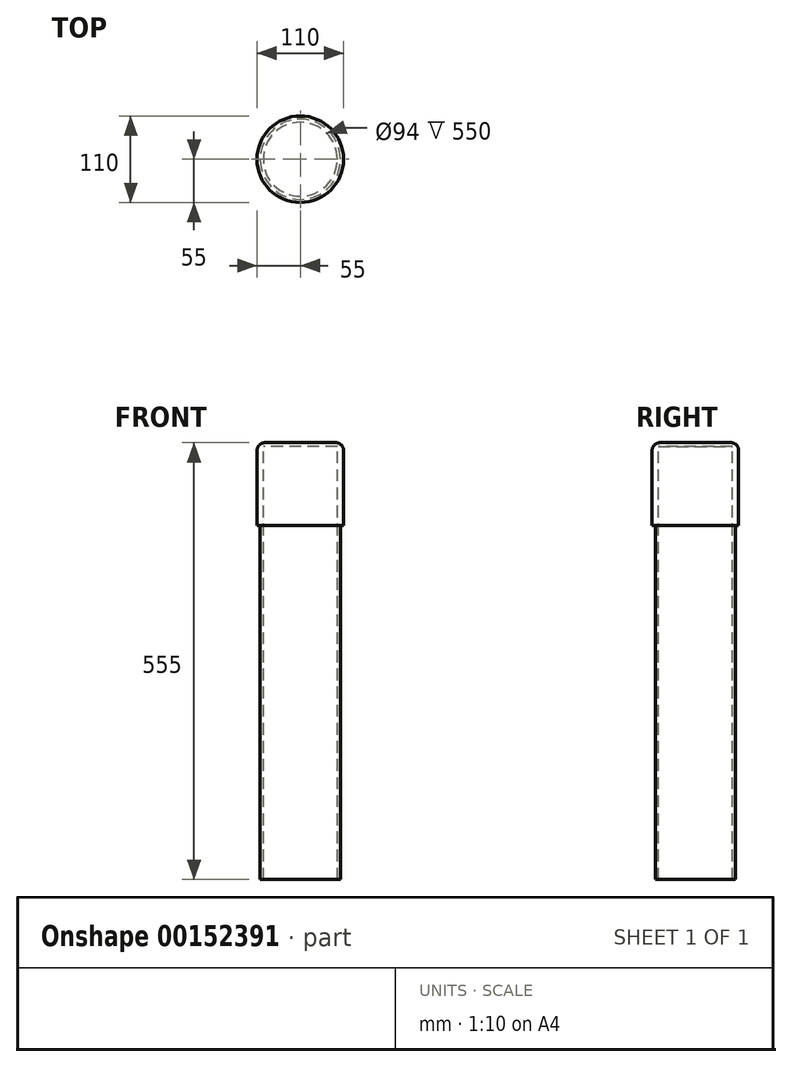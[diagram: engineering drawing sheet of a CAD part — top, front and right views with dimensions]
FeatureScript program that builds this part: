
annotation { "Feature Type Name" : "Feature", "Feature Type Description" : "" }
export const myFeature = defineFeature(function(context is Context, id is Id, definition is map)
    precondition{}
    {
        {
            var Q0;
            Q0=qCreatedBy(makeId("Top.planeOp"),FACE);
            var sketch = newSketch(context, id + "F0", { "sketchPlane" : qUnion([Q0])});
            skCircle(sketch, "E0", {"center": v(0, 0) * mm, "radius": 55 * mm});
            skCircle(sketch, "E1", {"center": v(0, 0) * mm, "radius": 51 * mm});
            skCircle(sketch, "E2", {"center": v(0, 0) * mm, "radius": 47 * mm});
            skSolve(sketch);
        }
        {
            var Q0;
            Q0=makeQuery(id+"F0.imprint","IMPRINT",FACE,{"disambiguationData":[TD([[makeQuery(id+"F0.imprint","IMPRINT",EDGE,{"derivedFrom":sQuery(id+"F0.wireOp",EDGE,"E1")}),1.0]])]});
            var Q1;
            Q1=makeQuery(id+"F0.imprint","IMPRINT",FACE,{"disambiguationData":[TD([[makeQuery(id+"F0.imprint","IMPRINT",EDGE,{"derivedFrom":sQuery(id+"F0.wireOp",EDGE,"E0")}),1.0]])]});
            var Q2;
            Q2=makeQuery(id+"F0.imprint","IMPRINT",FACE,{"disambiguationData":[TD([[makeQuery(id+"F0.imprint","IMPRINT",EDGE,{"derivedFrom":sQuery(id+"F0.wireOp",EDGE,"E2")}),1.0]])]});
            extrude(context, id + "F1", {"entities" : qUnion([Q0, Q1, Q2]), "depth" : 5 * mm});
        }
        {
            var Q0;
            Q0=makeQuery(id+"F0.imprint","IMPRINT",FACE,{"disambiguationData":[TD([[makeQuery(id+"F0.imprint","IMPRINT",EDGE,{"derivedFrom":sQuery(id+"F0.wireOp",EDGE,"E1")}),1.0]])]});
            extrude(context, id + "F2", {"entities" : qUnion([Q0]), "operationType" : NewBodyOperationType.ADD, "oppositeDirection" : true, "depth" : 50 * mm});
        }
        {
            var Q0;
            Q0=makeQuery(id+"F0.imprint","IMPRINT",FACE,{"disambiguationData":[TD([[makeQuery(id+"F0.imprint","IMPRINT",EDGE,{"derivedFrom":sQuery(id+"F0.wireOp",EDGE,"E0")}),1.0]])]});
            extrude(context, id + "F3", {"entities" : qUnion([Q0]), "operationType" : NewBodyOperationType.ADD, "oppositeDirection" : true, "depth" : 100 * mm});
        }
        {
            var Q0;
            Q0=makeQuery(id+"F1.opExtrude","CAP_EDGE",EDGE,{"disambiguationData":[OSD([sQuery(id+"F0.wireOp",EDGE,"E0")])],"isStart":false});
            fillet(context, id + "F4", {"entities" : qUnion([Q0]), "radius" : 10 * mm, "tangentPropagation" : true, "allowEdgeOverflow" : false});
        }
        {
            var Q0;
            Q0=makeQuery(id+"F2.opExtrude","CAP_FACE",FACE,{"disambiguationData":[OSD([sQuery(id+"F0.wireOp",EDGE,"E1"),sQuery(id+"F0.wireOp",EDGE,"E2")])],"isStart":false});
            extrude(context, id + "F5", {"entities" : qUnion([Q0]), "operationType" : NewBodyOperationType.ADD, "depth" : 500 * mm});
        }
        {
            var Q0;
            Q0=makeQuery(id+"F3.opExtrude","CAP_FACE",FACE,{"disambiguationData":[OSD([sQuery(id+"F0.wireOp",EDGE,"E0"),sQuery(id+"F0.wireOp",EDGE,"E1")])],"isStart":false});
            extrude(context, id + "F6", {"entities" : qUnion([Q0]), "operationType" : NewBodyOperationType.ADD, "oppositeDirection" : true, "depth" : 50 * mm});
        }
    });
